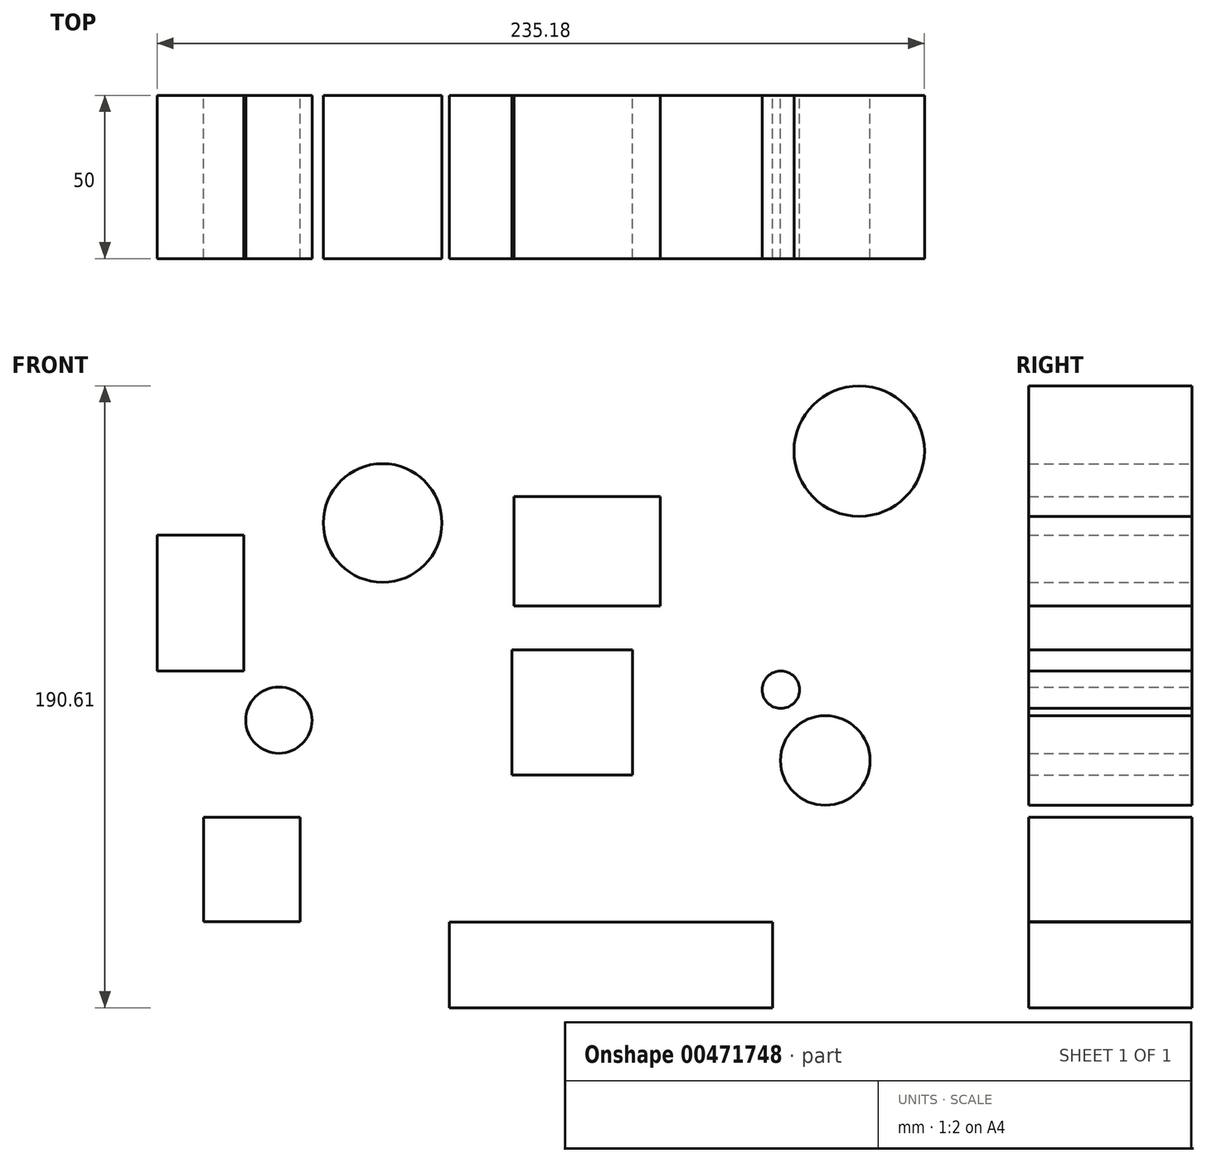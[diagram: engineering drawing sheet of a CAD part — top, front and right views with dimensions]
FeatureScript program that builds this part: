
annotation { "Feature Type Name" : "Feature", "Feature Type Description" : "" }
export const myFeature = defineFeature(function(context is Context, id is Id, definition is map)
    precondition{}
    {
        {
            var Q0;
            Q0=qCreatedBy(makeId("Front.planeOp"),FACE);
            var sketch = newSketch(context, id + "F0", { "sketchPlane" : qUnion([Q0])});
            skLineSegment(sketch, "E0.bottom", {"start": v(-81.63, 77.7) * mm, "end": v(-55.01, 77.7) * mm});
            skLineSegment(sketch, "E0.top", {"start": v(-81.63, 36.05) * mm, "end": v(-55.01, 36.05) * mm});
            skLineSegment(sketch, "E0.left", {"start": v(-81.63, 77.7) * mm, "end": v(-81.63, 36.05) * mm});
            skLineSegment(sketch, "E0.right", {"start": v(-55.01, 77.7) * mm, "end": v(-55.01, 36.05) * mm});
            skLineSegment(sketch, "E1.bottom", {"start": v(27.75, 89.47) * mm, "end": v(72.54, 89.47) * mm});
            skLineSegment(sketch, "E1.top", {"start": v(27.75, 56) * mm, "end": v(72.54, 56) * mm});
            skLineSegment(sketch, "E1.left", {"start": v(27.75, 89.47) * mm, "end": v(27.75, 56) * mm});
            skLineSegment(sketch, "E1.right", {"start": v(72.54, 89.47) * mm, "end": v(72.54, 56) * mm});
            skLineSegment(sketch, "E2.bottom", {"start": v(27.1, 42.55) * mm, "end": v(64.1, 42.55) * mm});
            skLineSegment(sketch, "E2.top", {"start": v(27.1, 4.22) * mm, "end": v(64.1, 4.22) * mm});
            skLineSegment(sketch, "E2.left", {"start": v(27.1, 42.55) * mm, "end": v(27.1, 4.22) * mm});
            skLineSegment(sketch, "E2.right", {"start": v(64.1, 42.55) * mm, "end": v(64.1, 4.22) * mm});
            skLineSegment(sketch, "E3.bottom", {"start": v(-67.35, -8.73) * mm, "end": v(-37.81, -8.73) * mm});
            skLineSegment(sketch, "E3.top", {"start": v(-67.35, -40.77) * mm, "end": v(-37.81, -40.77) * mm});
            skLineSegment(sketch, "E3.left", {"start": v(-67.35, -8.73) * mm, "end": v(-67.35, -40.77) * mm});
            skLineSegment(sketch, "E3.right", {"start": v(-37.81, -8.73) * mm, "end": v(-37.81, -40.77) * mm});
            skLineSegment(sketch, "E4.bottom", {"start": v(7.95, -40.87) * mm, "end": v(106.94, -40.87) * mm});
            skLineSegment(sketch, "E4.top", {"start": v(7.95, -67.15) * mm, "end": v(106.94, -67.15) * mm});
            skLineSegment(sketch, "E4.left", {"start": v(7.95, -40.87) * mm, "end": v(7.95, -67.15) * mm});
            skLineSegment(sketch, "E4.right", {"start": v(106.94, -40.87) * mm, "end": v(106.94, -67.15) * mm});
            skCircle(sketch, "E5", {"center": v(-12.5, 81.43) * mm, "radius": 18.18 * mm});
            skCircle(sketch, "E6", {"center": v(-44.3, 20.97) * mm, "radius": 10.15 * mm});
            skCircle(sketch, "E7", {"center": v(109.54, 30.32) * mm, "radius": 5.73 * mm});
            skCircle(sketch, "E8", {"center": v(123.17, 8.62) * mm, "radius": 13.73 * mm});
            skCircle(sketch, "E9", {"center": v(133.56, 103.47) * mm, "radius": 20 * mm});
            skSolve(sketch);
        }
        {
            var Q0;
            Q0 = qSketchRegion(id + "F0", true);
            extrude(context, id + "F1", {"entities" : qUnion([Q0]), "depth" : 25 * mm});
        }
        {
            var Q0;
            Q0=makeQuery(id+"F1.opExtrude","CAP_FACE",FACE,{"disambiguationData":[OSD([sQuery(id+"F0.wireOp",EDGE,"E0.bottom"),sQuery(id+"F0.wireOp",EDGE,"E0.top"),sQuery(id+"F0.wireOp",EDGE,"E0.left"),sQuery(id+"F0.wireOp",EDGE,"E0.right")])],"isStart":false});
            var Q1;
            Q1=makeQuery(id+"F1.opExtrude","CAP_FACE",FACE,{"disambiguationData":[OSD([sQuery(id+"F0.wireOp",EDGE,"E1.bottom"),sQuery(id+"F0.wireOp",EDGE,"E1.top"),sQuery(id+"F0.wireOp",EDGE,"E1.left"),sQuery(id+"F0.wireOp",EDGE,"E1.right")])],"isStart":false});
            var Q2;
            Q2=makeQuery(id+"F1.opExtrude","CAP_FACE",FACE,{"disambiguationData":[OSD([sQuery(id+"F0.wireOp",EDGE,"E5")])],"isStart":false});
            var Q3;
            Q3=makeQuery(id+"F1.opExtrude","CAP_FACE",FACE,{"disambiguationData":[OSD([sQuery(id+"F0.wireOp",EDGE,"E6")])],"isStart":false});
            var Q4;
            Q4=makeQuery(id+"F1.opExtrude","CAP_FACE",FACE,{"disambiguationData":[OSD([sQuery(id+"F0.wireOp",EDGE,"E3.bottom"),sQuery(id+"F0.wireOp",EDGE,"E3.top"),sQuery(id+"F0.wireOp",EDGE,"E3.left"),sQuery(id+"F0.wireOp",EDGE,"E3.right")])],"isStart":false});
            var Q5;
            Q5=makeQuery(id+"F1.opExtrude","CAP_FACE",FACE,{"disambiguationData":[OSD([sQuery(id+"F0.wireOp",EDGE,"E4.bottom"),sQuery(id+"F0.wireOp",EDGE,"E4.top"),sQuery(id+"F0.wireOp",EDGE,"E4.left"),sQuery(id+"F0.wireOp",EDGE,"E4.right")])],"isStart":false});
            var Q6;
            Q6=makeQuery(id+"F1.opExtrude","CAP_FACE",FACE,{"disambiguationData":[OSD([sQuery(id+"F0.wireOp",EDGE,"E8")])],"isStart":false});
            var Q7;
            Q7=makeQuery(id+"F1.opExtrude","CAP_FACE",FACE,{"disambiguationData":[OSD([sQuery(id+"F0.wireOp",EDGE,"E2.bottom"),sQuery(id+"F0.wireOp",EDGE,"E2.top"),sQuery(id+"F0.wireOp",EDGE,"E2.left"),sQuery(id+"F0.wireOp",EDGE,"E2.right")])],"isStart":false});
            var Q8;
            Q8=makeQuery(id+"F1.opExtrude","CAP_FACE",FACE,{"disambiguationData":[OSD([sQuery(id+"F0.wireOp",EDGE,"E7")])],"isStart":false});
            var Q9;
            Q9=makeQuery(id+"F1.opExtrude","CAP_FACE",FACE,{"disambiguationData":[OSD([sQuery(id+"F0.wireOp",EDGE,"E9")])],"isStart":false});
            extrude(context, id + "F2", {"entities" : qUnion([Q0, Q1, Q2, Q3, Q4, Q5, Q6, Q7, Q8, Q9]), "operationType" : NewBodyOperationType.ADD, "depth" : 25 * mm});
        }
    });
